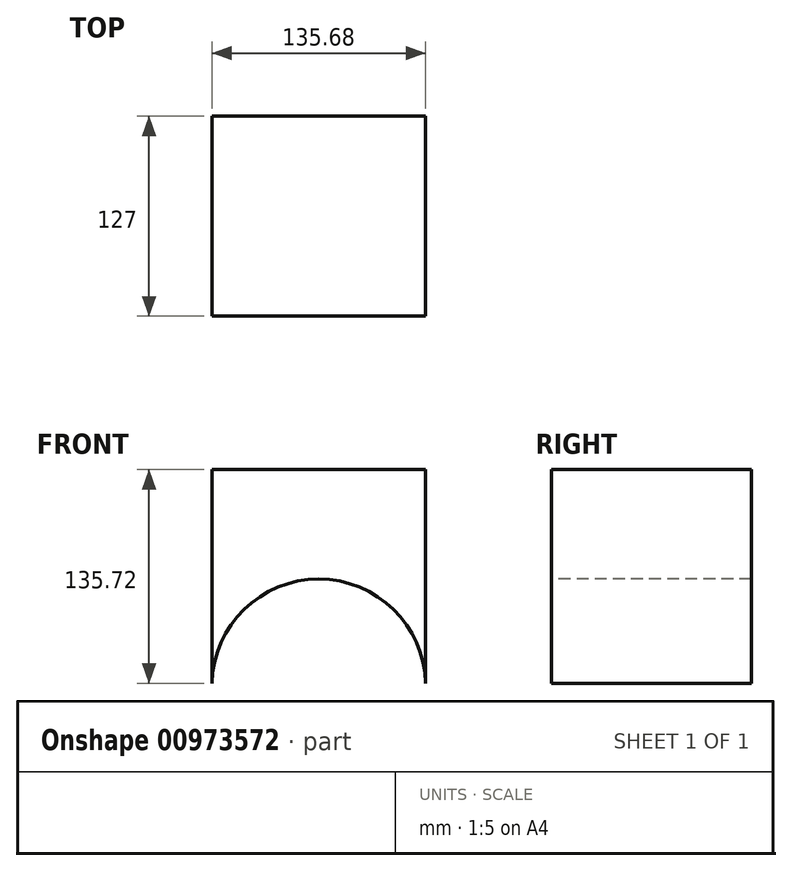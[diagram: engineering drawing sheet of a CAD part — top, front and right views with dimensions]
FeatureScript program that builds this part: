
annotation { "Feature Type Name" : "Feature", "Feature Type Description" : "" }
export const myFeature = defineFeature(function(context is Context, id is Id, definition is map)
    precondition{}
    {
        {
            var Q0;
            Q0=qCreatedBy(makeId("Front.planeOp"),FACE);
            var sketch = newSketch(context, id + "F0", { "sketchPlane" : qUnion([Q0])});
            skLineSegment(sketch, "E0.bottom", {"start": v(-67.84, 69.5) * mm, "end": v(67.84, 69.5) * mm});
            skLineSegment(sketch, "E0.top", {"start": v(-67.84, -69.5) * mm, "end": v(67.84, -69.5) * mm});
            skLineSegment(sketch, "E0.left", {"start": v(-67.84, 69.5) * mm, "end": v(-67.84, -69.5) * mm});
            skLineSegment(sketch, "E0.right", {"start": v(67.84, 69.5) * mm, "end": v(67.84, -69.5) * mm});
            skPoint(sketch, "E0.middle", {"position": v(0, 0) * mm});
            skSolve(sketch);
        }
        {
            var Q0;
            Q0=makeQuery(id+"F0.imprint","IMPRINT",FACE,{"disambiguationData":[TD([[makeQuery(id+"F0.imprint","IMPRINT",EDGE,{"derivedFrom":sQuery(id+"F0.wireOp",EDGE,"E0.bottom")}),-1.0]])]});
            extrude(context, id + "F1", {"entities" : qUnion([Q0]), "depth" : 127 * mm, "offsetDistance" : 25.4 * mm});
        }
        {
            var Q0;
            Q0=makeQuery(id+"F1.opExtrude","CAP_FACE",FACE,{"disambiguationData":[OSD([sQuery(id+"F0.wireOp",EDGE,"E0.bottom"),sQuery(id+"F0.wireOp",EDGE,"E0.top"),sQuery(id+"F0.wireOp",EDGE,"E0.left"),sQuery(id+"F0.wireOp",EDGE,"E0.right")])],"isStart":false});
            var sketch = newSketch(context, id + "F2", { "sketchPlane" : qUnion([Q0])});
            skArc(sketch, "E1", {"start": v(67.84, -69.5) * mm, "mid": v(0, 0) * mm, "end": v(-67.84, -69.5) * mm});
            skSolve(sketch);
        }
        {
            var Q0;
            {var subQ5=makeQuery(id+"F1.opExtrude","CAP_EDGE",EDGE,{"disambiguationData":[OSD([sQuery(id+"F0.wireOp",EDGE,"E0.top")])],"isStart":false});Q0=makeQuery(id+"F2.imprint","IMPRINT",FACE,{"disambiguationData":[TD([[makeQuery(id+"F2.imprint","IMPRINT",EDGE,{"derivedFrom":subQ5}),1.0]])]});}
            extrude(context, id + "F3", {"entities" : qUnion([Q0]), "operationType" : NewBodyOperationType.REMOVE, "oppositeDirection" : true, "depth" : 127 * mm, "offsetDistance" : 25.4 * mm});
        }
    });
